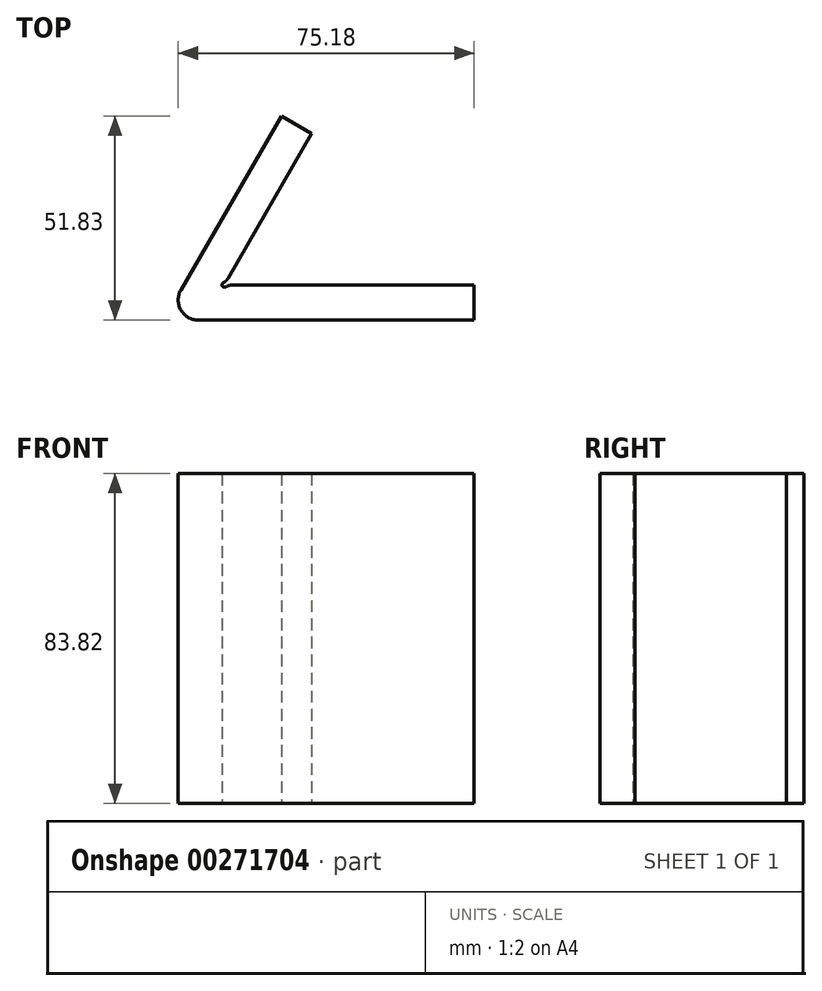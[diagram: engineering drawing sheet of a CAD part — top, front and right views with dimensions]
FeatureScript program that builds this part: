
annotation { "Feature Type Name" : "Feature", "Feature Type Description" : "" }
export const myFeature = defineFeature(function(context is Context, id is Id, definition is map)
    precondition{}
    {
        {
            var Q0;
            Q0=qCreatedBy(makeId("Top.planeOp"),FACE);
            var sketch = newSketch(context, id + "F0", { "sketchPlane" : qUnion([Q0])});
            skLineSegment(sketch, "E0", {"start": v(8.8, 0) * mm, "end": v(78.9, 0) * mm});
            skLineSegment(sketch, "E1", {"start": v(78.9, 0) * mm, "end": v(78.9, 8.89) * mm});
            skLineSegment(sketch, "E2", {"start": v(78.9, 8.89) * mm, "end": v(15.4, 8.89) * mm});
            skLineSegment(sketch, "E3", {"start": v(15.4, 8.89) * mm, "end": v(37.62, 47.38) * mm});
            skLineSegment(sketch, "E4", {"start": v(37.62, 47.38) * mm, "end": v(29.92, 51.83) * mm});
            skLineSegment(sketch, "E5", {"start": v(29.92, 51.83) * mm, "end": v(4.4, 7.62) * mm});
            skPoint(sketch, "E6", {"position": v(34.45, 8.89) * mm});
            skLineSegment(sketch, "E7", {"start": v(34.45, 8.89) * mm, "end": v(85.1, 96.63) * mm, "construction": true});
            skPoint(sketch, "E8.visualSharp", {"position": v(0, 0) * mm});
            skArc(sketch, "E8.filletArc", {"start": v(4.4, 7.62) * mm, "mid": v(4.4, 2.54) * mm, "end": v(8.8, 0) * mm});
            skLineSegment(sketch, "E9", {"start": v(16.03, 9.99) * mm, "end": v(15.2, 9.5) * mm});
            skLineSegment(sketch, "E10", {"start": v(15.2, 9.5) * mm, "end": v(15.83, 8.4) * mm, "construction": true});
            skLineSegment(sketch, "E11", {"start": v(15.83, 8.4) * mm, "end": v(16.67, 8.89) * mm});
            skLineSegment(sketch, "E12", {"start": v(15.5, 8.95) * mm, "end": v(21.5, 12.41) * mm, "construction": true});
            skArc(sketch, "E13", {"start": v(15.2, 9.5) * mm, "mid": v(14.96, 8.64) * mm, "end": v(15.83, 8.4) * mm});
            skSolve(sketch);
        }
        {
            var Q0;
            Q0=makeQuery(id+"F0.imprint","IMPRINT",FACE,{"disambiguationData":[TD([[makeQuery(id+"F0.imprint","IMPRINT",EDGE,{"derivedFrom":sQuery(id+"F0.wireOp",EDGE,"E0")}),1.0]])]});
            extrude(context, id + "F1", {"entities" : qUnion([Q0]), "depth" : 83.82 * mm});
        }
        {
            var Q0;
            Q0=makeQuery(id+"F1.opExtrude","SWEPT_EDGE",EDGE,{"disambiguationData":[OSD([sQuery(id+"F0.wireOp",EDGE,"E3"),sQuery(id+"F0.wireOp",EDGE,"E9")])]});
            var Q1;
            Q1=makeQuery(id+"F1.opExtrude","SWEPT_EDGE",EDGE,{"disambiguationData":[OSD([sQuery(id+"F0.wireOp",EDGE,"E2"),sQuery(id+"F0.wireOp",EDGE,"E11")])]});
            fillet(context, id + "F2", {"entities" : qUnion([Q0, Q1]), "radius" : 2.54 * mm, "tangentPropagation" : true, "allowEdgeOverflow" : false});
        }
        {
            var Q0;
            Q0=makeQuery(id+"F1.opExtrude","CAP_FACE",FACE,{"disambiguationData":[OSD([sQuery(id+"F0.wireOp",EDGE,"E0"),sQuery(id+"F0.wireOp",EDGE,"E1"),sQuery(id+"F0.wireOp",EDGE,"E2"),sQuery(id+"F0.wireOp",EDGE,"E3"),sQuery(id+"F0.wireOp",EDGE,"E4"),sQuery(id+"F0.wireOp",EDGE,"E5"),sQuery(id+"F0.wireOp",EDGE,"E8.filletArc"),sQuery(id+"F0.wireOp",EDGE,"E9"),sQuery(id+"F0.wireOp",EDGE,"E11"),sQuery(id+"F0.wireOp",EDGE,"E13")])],"isStart":false});
            var Q1;
            Q1=makeQuery(id+"F1.opExtrude","CAP_FACE",FACE,{"disambiguationData":[OSD([sQuery(id+"F0.wireOp",EDGE,"E0"),sQuery(id+"F0.wireOp",EDGE,"E1"),sQuery(id+"F0.wireOp",EDGE,"E2"),sQuery(id+"F0.wireOp",EDGE,"E3"),sQuery(id+"F0.wireOp",EDGE,"E4"),sQuery(id+"F0.wireOp",EDGE,"E5"),sQuery(id+"F0.wireOp",EDGE,"E8.filletArc"),sQuery(id+"F0.wireOp",EDGE,"E9"),sQuery(id+"F0.wireOp",EDGE,"E11"),sQuery(id+"F0.wireOp",EDGE,"E13")])],"isStart":true});
            cPlane(context, id + "F3", {"entities" : qUnion([Q0, Q1]), "cplaneType" : CPlaneType.MID_PLANE, "offset" : 25.4 * mm, "width" : 152.4 * mm, "height" : 152.4 * mm});
        }
    });
